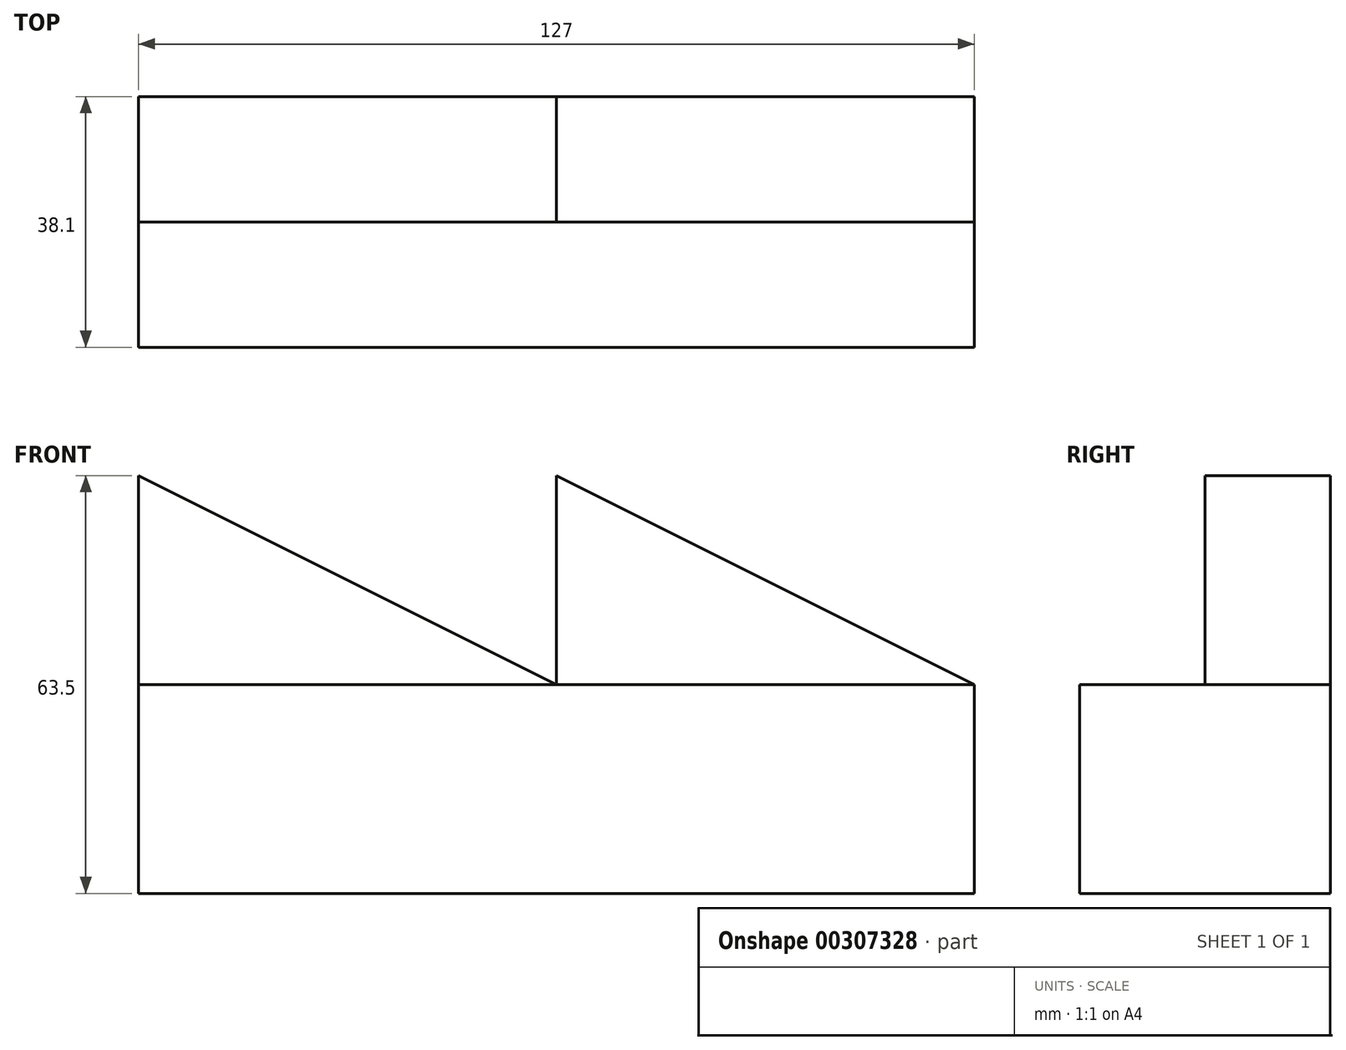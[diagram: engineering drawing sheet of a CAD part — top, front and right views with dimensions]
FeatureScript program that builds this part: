
annotation { "Feature Type Name" : "Feature", "Feature Type Description" : "" }
export const myFeature = defineFeature(function(context is Context, id is Id, definition is map)
    precondition{}
    {
        {
            var Q0;
            Q0=qCreatedBy(makeId("Front.planeOp"),FACE);
            var sketch = newSketch(context, id + "F0", { "sketchPlane" : qUnion([Q0])});
            skLineSegment(sketch, "E0", {"start": v(-25.64, -34.76) * mm, "end": v(101.36, -34.76) * mm});
            skLineSegment(sketch, "E1", {"start": v(101.36, -34.76) * mm, "end": v(101.36, -3) * mm});
            skLineSegment(sketch, "E2", {"start": v(101.36, -3) * mm, "end": v(-25.64, -3) * mm});
            skLineSegment(sketch, "E3", {"start": v(-25.64, -3) * mm, "end": v(-25.64, -34.76) * mm});
            skLineSegment(sketch, "E4", {"start": v(101.36, -3) * mm, "end": v(37.86, -3) * mm});
            skLineSegment(sketch, "E5", {"start": v(37.86, -3) * mm, "end": v(37.86, 28.74) * mm});
            skLineSegment(sketch, "E6", {"start": v(37.86, 28.74) * mm, "end": v(101.36, -3) * mm});
            skLineSegment(sketch, "E7", {"start": v(-25.64, -3) * mm, "end": v(-25.64, 28.74) * mm});
            skLineSegment(sketch, "E8", {"start": v(-25.64, 28.74) * mm, "end": v(37.86, -3) * mm});
            skSolve(sketch);
        }
        {
            var Q0;
            Q0=makeQuery(id+"F0.imprint","IMPRINT",FACE,{"disambiguationData":[TD([[makeQuery(id+"F0.imprint","IMPRINT",EDGE,{"derivedFrom":sQuery(id+"F0.wireOp",EDGE,"E0")}),1.0]])]});
            extrude(context, id + "F1", {"entities" : qUnion([Q0]), "depth" : 38.1 * mm});
        }
        {
            var Q0;
            Q0=makeQuery(id+"F0.imprint","IMPRINT",FACE,{"disambiguationData":[TD([[makeQuery(id+"F0.imprint","IMPRINT",EDGE,{"derivedFrom":sQuery(id+"F0.wireOp",EDGE,"E4")}),-1.0]])]});
            var Q1;
            Q1=makeQuery(id+"F0.imprint","IMPRINT",FACE,{"disambiguationData":[TD([[makeQuery(id+"F0.imprint","IMPRINT",EDGE,{"derivedFrom":sQuery(id+"F0.wireOp",EDGE,"E2")}),-1.0]])]});
            extrude(context, id + "F2", {"entities" : qUnion([Q0, Q1]), "operationType" : NewBodyOperationType.ADD, "depth" : 19.05 * mm});
        }
    });
